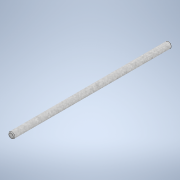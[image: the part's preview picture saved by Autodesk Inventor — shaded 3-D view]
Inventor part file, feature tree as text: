
AUTODESK INVENTOR PART (.ipt)
format: ipt  version: 2021.3 (Build 253353000, 353)  size: 101,888 bytes
history: native  units: mm
features: extrude x1, fillet x1, sketch x1
ambient origin geometry x8: Origin, YZ Plane, XZ Plane, XY Plane, X Axis, Y Axis, Z Axis, Center Point
bodies: Solid1 (feature_tree)
feature tree (3):
  extrude  "Extrusion1"  Depth=180.0mm TaperAngle=0.0deg
  fillet  "Fillet1"  Radius=1.0mm
  sketch  "Sketch1"  dims[d0=7.0mm d1=180.0mm d2=0.0mm d3=1.0mm]
